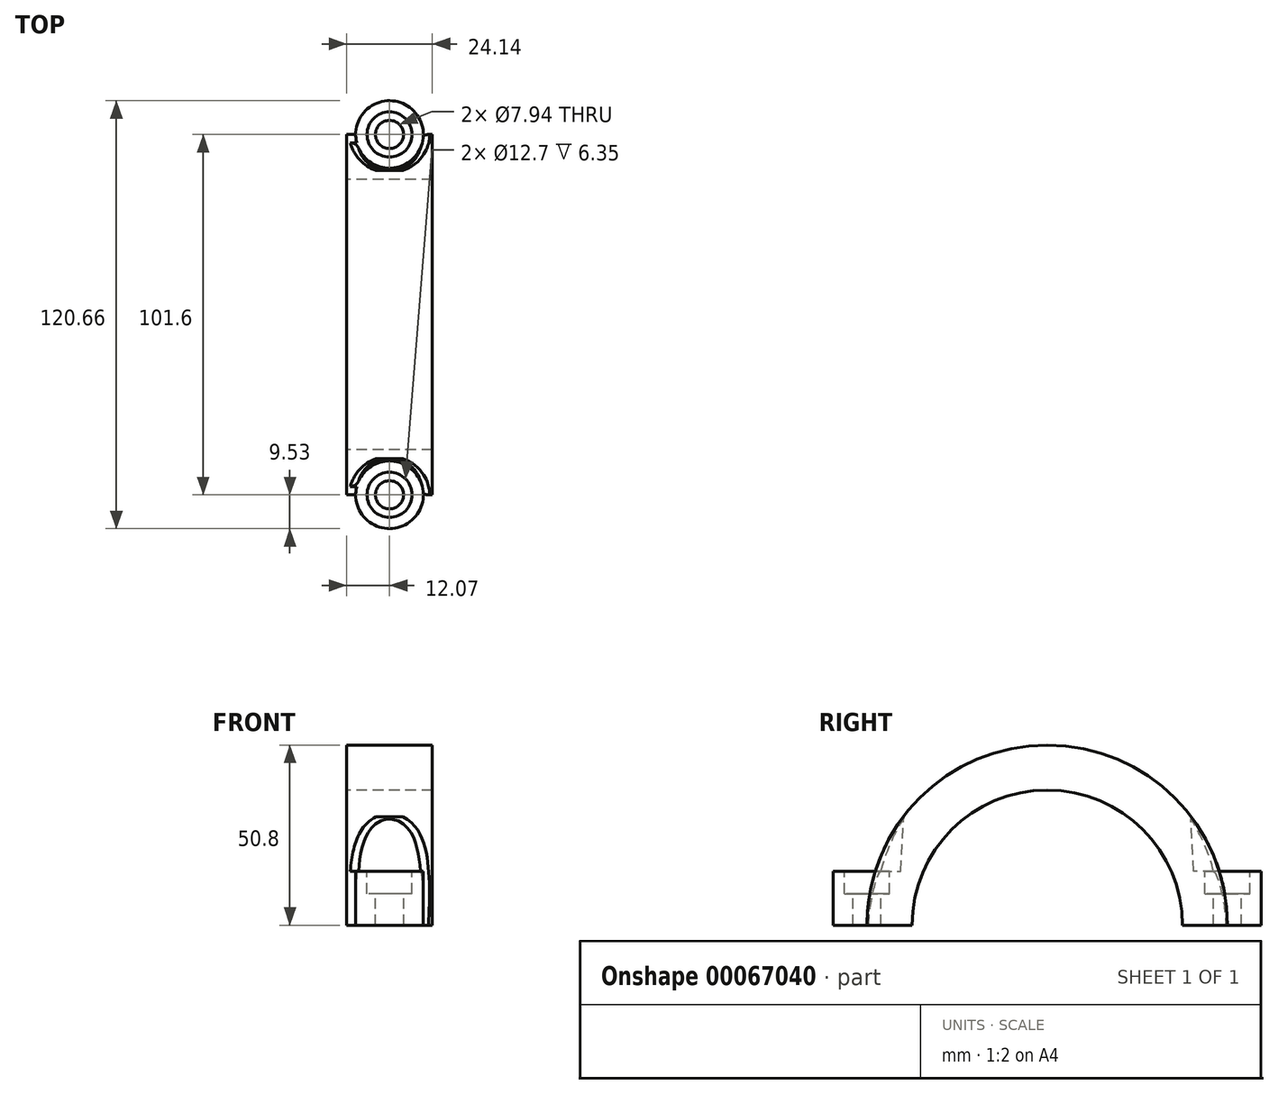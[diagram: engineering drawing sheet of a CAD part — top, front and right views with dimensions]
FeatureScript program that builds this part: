
annotation { "Feature Type Name" : "Feature", "Feature Type Description" : "" }
export const myFeature = defineFeature(function(context is Context, id is Id, definition is map)
    precondition{}
    {
        {
            var Q0;
            Q0=qCreatedBy(makeId("Right.planeOp"),FACE);
            var sketch = newSketch(context, id + "F0", { "sketchPlane" : qUnion([Q0])});
            skArc(sketch, "E0", {"start": v(38.1, 0) * mm, "mid": v(0, 38.1) * mm, "end": v(-38.1, 0) * mm});
            skArc(sketch, "E1.0", {"start": v(50.8, 0) * mm, "mid": v(0, 50.8) * mm, "end": v(-50.8, 0) * mm});
            skLineSegment(sketch, "E2.trimOffspring", {"start": v(38.1, 0) * mm, "end": v(50.8, 0) * mm});
            skLineSegment(sketch, "E3", {"start": v(-50.8, 0) * mm, "end": v(-38.1, 0) * mm});
            skSolve(sketch);
        }
        {
            var Q0;
            Q0=qSketchRegion(id+"F0",true);
            extrude(context, id + "F1", {"entities" : qUnion([Q0]), "endBound" : BoundingType.SYMMETRIC, "depth" : 24.13 * mm});
        }
        {
            var Q0;
            Q0=makeQuery(id+"F1.opExtrude","SWEPT_FACE",FACE,{"disambiguationData":[OSD([sQuery(id+"F0.wireOp",EDGE,"E3")])]});
            var sketch = newSketch(context, id + "F2", { "sketchPlane" : qUnion([Q0])});
            skCircle(sketch, "E4", {"center": v(0, -50.8) * mm, "radius": 9.53 * mm});
            skCircle(sketch, "E5", {"center": v(0, 50.8) * mm, "radius": 9.53 * mm});
            skSolve(sketch);
        }
        {
            var Q0;
            Q0=qSketchRegion(id+"F2",true);
            extrude(context, id + "F3", {"entities" : qUnion([Q0]), "operationType" : NewBodyOperationType.ADD, "oppositeDirection" : true, "depth" : 15.25 * mm});
        }
        {
            var Q0;
            Q0=makeQuery(id+"F3.opExtrude","CAP_FACE",FACE,{"disambiguationData":[OSD([sQuery(id+"F2.wireOp",EDGE,"E5")])],"isStart":false});
            var sketch = newSketch(context, id + "F4", { "sketchPlane" : qUnion([Q0])});
            skCircle(sketch, "E6", {"center": v(0, 50.8) * mm, "radius": 9.53 * mm});
            skCircle(sketch, "E7", {"center": v(0, -50.8) * mm, "radius": 9.53 * mm});
            skSolve(sketch);
        }
        {
            var Q0;
            Q0=qSketchRegion(id+"F4",true);
            extrude(context, id + "F5", {"entities" : qUnion([Q0]), "operationType" : NewBodyOperationType.REMOVE, "depth" : 15.25 * mm, "hasDraft" : true, "draftAngle" : 3 * degree});
        }
        {
            var Q0;
            Q0=makeQuery(id+"F5.boolean.opBoolean","MERGE",FACE,{"derivedFrom":[makeQuery(id+"F3.opExtrude","CAP_FACE",FACE,{"disambiguationData":[OSD([sQuery(id+"F2.wireOp",EDGE,"E4")])],"isStart":false}),makeQuery(id+"F5.opExtrude","CAP_FACE",FACE,{"disambiguationData":[OSD([sQuery(id+"F4.wireOp",EDGE,"E6")])],"isStart":true})]});
            var sketch = newSketch(context, id + "F6", { "sketchPlane" : qUnion([Q0])});
            skPoint(sketch, "E8", {"position": v(0, 50.8) * mm});
            skPoint(sketch, "E9", {"position": v(0, -50.8) * mm});
            skSolve(sketch);
        }
        {
            var Q0;
            Q0=makeQuery(id+"F5.boolean.opBoolean","INTERSECT",EDGE,{"disambiguationData":[OD(1.0)],"derivedFrom":[makeQuery(id+"F1.opExtrude","SWEPT_FACE",FACE,{"disambiguationData":[OSD([sQuery(id+"F0.wireOp",EDGE,"E1.0")])]}),makeQuery(id+"F5.opExtrude","SWEPT_FACE",FACE,{"disambiguationData":[OSD([sQuery(id+"F4.wireOp",EDGE,"E7")])]})]});
            fillet(context, id + "F7", {"entities" : qUnion([Q0]), "radius" : 2.54 * mm, "tangentPropagation" : true, "allowEdgeOverflow" : false});
        }
        {
            var Q0;
            Q0=makeQuery(id+"F5.boolean.opBoolean","INTERSECT",EDGE,{"disambiguationData":[OD(1.0)],"derivedFrom":[makeQuery(id+"F1.opExtrude","SWEPT_FACE",FACE,{"disambiguationData":[OSD([sQuery(id+"F0.wireOp",EDGE,"E1.0")])]}),makeQuery(id+"F5.opExtrude","SWEPT_FACE",FACE,{"disambiguationData":[OSD([sQuery(id+"F4.wireOp",EDGE,"E6")])]})]});
            fillet(context, id + "F8", {"entities" : qUnion([Q0]), "radius" : 2.54 * mm, "tangentPropagation" : true, "allowEdgeOverflow" : false});
        }
        {
            var Q0;
            Q0=sQuery(id+"F6.wireOp",VERTEX,"E8");
            var Q1;
            Q1=sQuery(id+"F6.wireOp",VERTEX,"E9");
            var Q2;
            Q2=makeQuery(id+"F1.opExtrude","SWEPT_BODY",BODY,{"disambiguationData":[OSD([sQuery(id+"F0.wireOp",EDGE,"E0"),sQuery(id+"F0.wireOp",EDGE,"E1.0"),sQuery(id+"F0.wireOp",EDGE,"E2.trimOffspring"),sQuery(id+"F0.wireOp",EDGE,"E3")])]});
            hole(context, id + "F9", {"style" : HoleStyle.C_BORE, "holeDiameter" : 7.94 * mm, "cBoreDiameter" : 12.7 * mm, "cBoreDepth" : 6.35 * mm, "endStyle" : HoleEndStyle.THROUGH, "locations" : qUnion([Q0, Q1]), "scope" : qUnion([Q2])});
        }
    });
